# Revit family: 117 PLUS - Corner Panel - Internal Deflection Head (+- 25mm or +- 40mm)
name_source: partatom
category: Curtain Panels
revit_build: Autodesk Revit 2013 (Build: 20120221_2030(x64)
units: mm (PartAtom-declared; Revit-internal decimal feet)

## types (1)
- 117 PLUS - Corner Panel - Internal Deflection Head (+- 25mm or +- 40mm)
    36 = 36 mm  [stored 0.11811 ft]
    Abutment Track Depth = 25 mm  [stored 0.082021 ft]
    Abutment Track Material = Aluminum
    Acoustic Single Glazed = 12mm Toughened: Rw33dB, 10.4mm Laminate: Rw35dB, 10.8mm Acoustic Laminate: Rw37dB, 12.8mm Acoustic Laminate: Rw38dB
    Base Track Height = 25 mm  [stored 0.082021 ft]
    Base Track Material = Aluminum
    Corner Joint Material = <By Category>
    Description = Start/End Panel:+-25mm & +- 40mm Deflection Head with Floor & Abutment Tracks
    Glass Joints = Glass to glass joints: Nebula, Tape, Aluminium & PETG
    Glass Material = Glass
    Glass Thickness = 13 mm  [stored 0.0426509 ft]
    Head Deflection = 25 mm  [stored 0.082021 ft]
    Head Track (Lower) Height = 65 mm  [stored 0.213255 ft]
    Head Track (Lower) Material = Aluminum
    Head Track (Upper) Material = Aluminum
    Manufacturer = Optima Products Ltd.
    Model = Optima 117 Plus
    Nebula Joint = Yes
    Taped Joint = Yes
    Track Width = 36 mm  [stored 0.11811 ft]
    Type Comments = Head Tracks: 117102-01(90mm) & 117104-01 (135mm) | Base Tracks: 117108-01(50mm), 117108-02(40mm), 117108-03 (25mm) | Abutment Tracks: 117112-01 (50mm), 117112-02 (40mm), 117112-03 (25mm)
    URL = http://www.optimasystems.com

note: [stored X ft] marks values corroborated as IEEE doubles in the binary element streams (Revit-internal decimal feet)

## geometry (parser evidence)
native form markers: Blend x4, Extrusion x1, Sweep x1
no freeform markers — native parametric forms only
